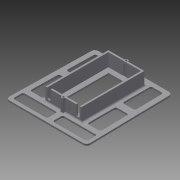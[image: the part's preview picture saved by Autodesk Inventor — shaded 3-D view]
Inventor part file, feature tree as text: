
AUTODESK INVENTOR PART (.ipt)
format: ipt  version: 2014 SP1 (Build 180222100, 222)  size: 296,448 bytes
history: native  units: in
note: dims shown in document units (in); Inventor stores cm internally (conversion verified against a paired STEP export)
features: extrude x11, sketch x10, fillet x3
ambient origin geometry x8: Origin, YZ Plane, XZ Plane, XY Plane, X Axis, Y Axis, Z Axis, Center Point
bodies: Solid1 (feature_tree)
feature tree (24):
  extrude  "Extrusion1"  Depth=0.25in
  fillet  "Fillet1"  Radius=4.34in
  extrude  "Extrusion4"  Depth=0.125in TaperAngle=0.0deg
  extrude  "Extrusion5"  Depth=0.1in TaperAngle=0.0deg
  extrude  "Extrusion6"  Depth=0.125in
  extrude  "Extrusion9"  Depth=0.125in
  extrude  "Extrusion10"  Depth=0.125in
  fillet  "Fillet3"  Radius=0.01in
  extrude  "Extrusion15"  Depth=0.125in
  extrude  "Extrusion16"  Depth=6.375in
  fillet  "Fillet4"  Radius=5.65in
  extrude  "Extrusion18"  Depth=2.625in
  extrude  "Extrusion20"  Depth=0.125in
  extrude  "Extrusion21"  Depth=0.12in TaperAngle=0.0deg
  sketch  "Sketch4"  dims[d2=0.12in d3=0.0in d4=0.25in d12=4.34in]
  sketch  "Sketch5"  dims[d15=0.95in d16=0.0in d17=0.125in d18=0.0in]
  sketch  "Sketch6"  dims[d19=5.0in d20=0.0in d26=0.1in d27=0.0in]
  sketch  "Sketch9"  dims[d29=1.0in d30=0.0in d43=0.125in]
  sketch  "Sketch10"  dims[d48=0.818in d49=0.0in d50=0.125in]
  sketch  "Sketch15"  dims[d51=0.125in d52=0.125in d58=0.01in]
  sketch  "Sketch16"  dims[d59=5.0in d60=0.0in d67=0.125in]
  sketch  "Sketch19"  dims[d71=0.25in d74=6.375in d75=5.65in]
  sketch  "Sketch21"  dims[d76=5.9in d78=2.625in]
  sketch  "Sketch22"  dims[d81=0.12in d82=0.0in d97=0.125in d98=0.12in d99=0.0in d107=0.125in d108=0.125in d109=0.12in d110=0.0in d111=0.75in d112=0.75in d113=2.5in d114=2.5in d122=0.1625in d123=0.1625in d124=0.1625in d126=0.535in d127=0.125in]
